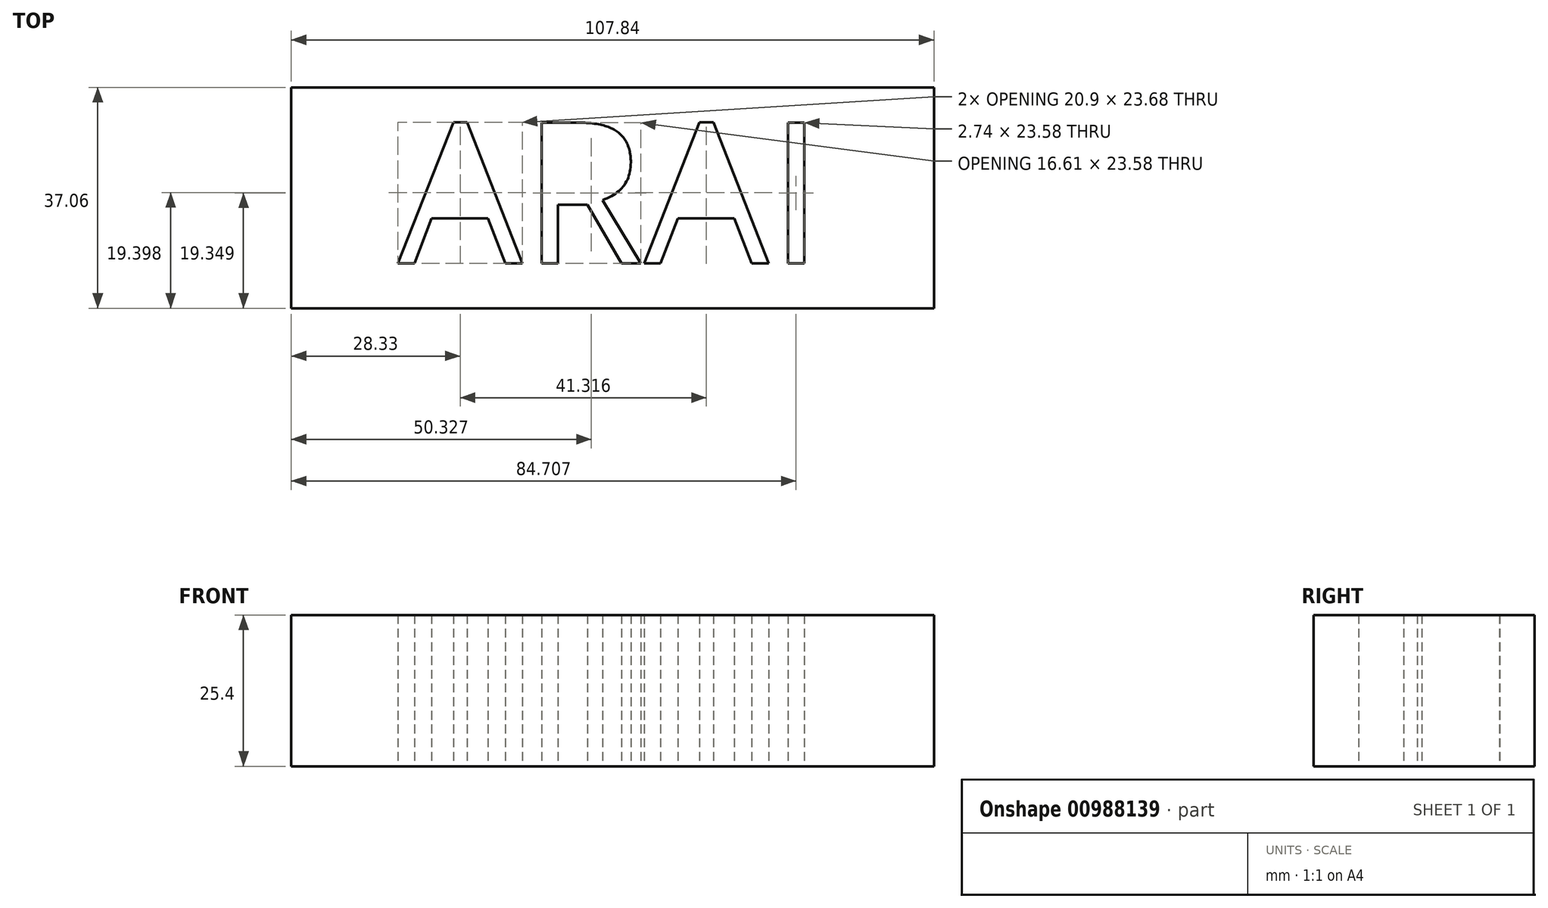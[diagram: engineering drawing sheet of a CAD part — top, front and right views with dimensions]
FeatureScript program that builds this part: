
annotation { "Feature Type Name" : "Feature", "Feature Type Description" : "" }
export const myFeature = defineFeature(function(context is Context, id is Id, definition is map)
    precondition{}
    {
        {
            var Q0;
            Q0=qCreatedBy(makeId("Top.planeOp"),FACE);
            var sketch = newSketch(context, id + "F0", { "sketchPlane" : qUnion([Q0])});
            skLineSegment(sketch, "E0.bottom", {"start": v(-53.92, 18.53) * mm, "end": v(53.92, 18.53) * mm});
            skLineSegment(sketch, "E0.top", {"start": v(-53.92, -18.53) * mm, "end": v(53.92, -18.53) * mm});
            skLineSegment(sketch, "E0.left", {"start": v(-53.92, 18.53) * mm, "end": v(-53.92, -18.53) * mm});
            skLineSegment(sketch, "E0.right", {"start": v(53.92, 18.53) * mm, "end": v(53.92, -18.53) * mm});
            skPoint(sketch, "E0.middle", {"position": v(0, 0) * mm});
            skText(sketch, "E1", { "text": "ARAI", "fontName": "OpenSans-Regular.ttf"});
            const initialGuessF0  = {"E1": [-0.03604, -0.01097, 1, 0, 0.02378]};
            skSetInitialGuess(sketch, initialGuessF0);
            skSolve(sketch);
        }
        {
            var Q0;
            Q0=makeQuery(id+"F0.imprint","IMPRINT",FACE,{"disambiguationData":[TD([[makeQuery(id+"F0.imprint","IMPRINT",EDGE,{"derivedFrom":sQuery(id+"F0.wireOp",EDGE,"E0.bottom")}),-1.0]])]});
            extrude(context, id + "F1", {"entities" : qUnion([Q0]), "depth" : 25.4 * mm, "offsetDistance" : 25.4 * mm});
        }
    });
